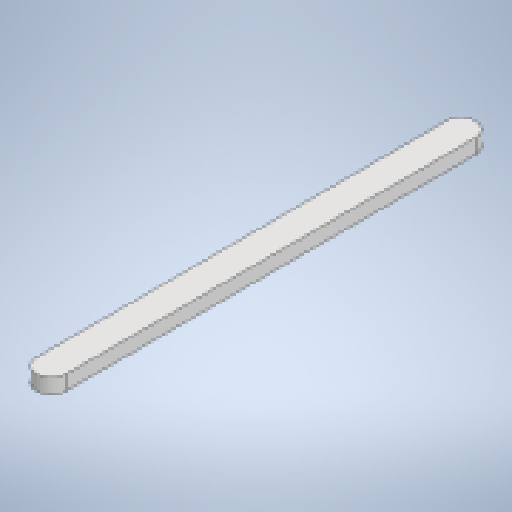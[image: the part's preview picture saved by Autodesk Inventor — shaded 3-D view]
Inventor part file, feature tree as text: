
AUTODESK INVENTOR PART (.ipt)
format: ipt  version: 2024 (Build 280153000, 153)  size: 179,200 bytes
history: native  units: in
note: dims shown in document units (in); Inventor stores cm internally (conversion verified against a paired STEP export)
features: extrude x1, sketch x1
ambient origin geometry x8: Origin, YZ Plane, XZ Plane, XY Plane, X Axis, Y Axis, Z Axis, Center Point
bodies: Solid1 (feature_tree)
feature tree (2):
  extrude  "Extrusion1"  Depth=0.0625in
  sketch  "Sketch1"  dims[d2=0.0625in d3=0.0in d4=0.2165in d5=0.1181in d6=0.1181in d7=0.9449in d8=0.2165in d9=0.0118in d10=0.3346in d11=0.8268in d12=0.1575in d13=1.75in d14=0.125in d15=0.125in d16=0.0079in]
